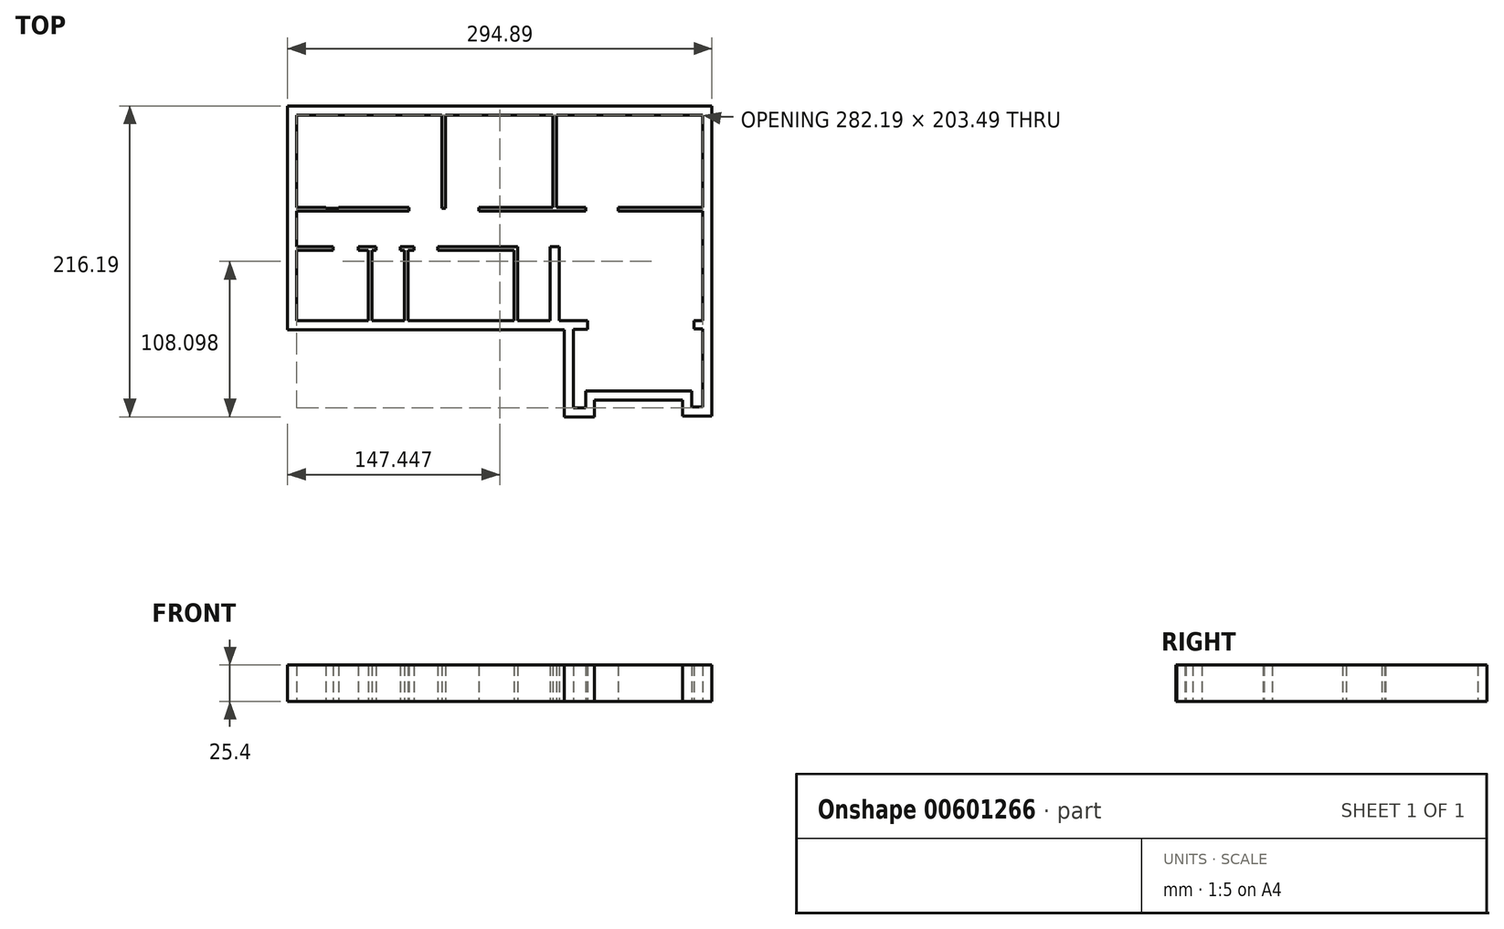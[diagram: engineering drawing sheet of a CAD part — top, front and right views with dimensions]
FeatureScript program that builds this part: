
annotation { "Feature Type Name" : "Feature", "Feature Type Description" : "" }
export const myFeature = defineFeature(function(context is Context, id is Id, definition is map)
    precondition{}
    {
        {
            var Q0;
            Q0=qCreatedBy(makeId("Top.planeOp"),FACE);
            var sketch = newSketch(context, id + "F0", { "sketchPlane" : qUnion([Q0])});
            skLineSegment(sketch, "E0.bottom", {"start": v(0, 66.8) * mm, "end": v(282.2, 66.8) * mm});
            skLineSegment(sketch, "E0.left", {"start": v(0, 66.8) * mm, "end": v(0, -76.2) * mm});
            skLineSegment(sketch, "E0.right", {"start": v(282.2, 66.8) * mm, "end": v(282.2, -81.91) * mm});
            skPoint(sketch, "E1.oppositeSnap0", {"position": v(180.6, 0) * mm});
            skLineSegment(sketch, "E1.right", {"start": v(282.2, 2.54) * mm, "end": v(282.2, 0) * mm});
            skLineSegment(sketch, "E2.bottom", {"start": v(100.84, 66.8) * mm, "end": v(103.38, 66.8) * mm});
            skLineSegment(sketch, "E2.top", {"start": v(100.84, 2.08) * mm, "end": v(103.38, 2.08) * mm});
            skLineSegment(sketch, "E2.left", {"start": v(100.84, 66.8) * mm, "end": v(100.84, 2.08) * mm});
            skLineSegment(sketch, "E2.right", {"start": v(103.38, 66.8) * mm, "end": v(103.38, 2.08) * mm});
            skLineSegment(sketch, "E3.bottom", {"start": v(178.05, 66.8) * mm, "end": v(180.6, 66.8) * mm});
            skLineSegment(sketch, "E3.top", {"start": v(178.05, 2.54) * mm, "end": v(180.6, 2.54) * mm});
            skLineSegment(sketch, "E3.left", {"start": v(178.05, 66.8) * mm, "end": v(178.05, 2.54) * mm});
            skLineSegment(sketch, "E3.right", {"start": v(180.6, 66.8) * mm, "end": v(180.6, 2.54) * mm});
            skLineSegment(sketch, "E4.left", {"start": v(0, -24.64) * mm, "end": v(0, -27.18) * mm});
            skLineSegment(sketch, "E5.bottom", {"start": v(176.02, -24.64) * mm, "end": v(182.37, -24.64) * mm});
            skLineSegment(sketch, "E5.top", {"start": v(176.02, -76.2) * mm, "end": v(182.37, -76.2) * mm});
            skLineSegment(sketch, "E5.left", {"start": v(176.02, -24.64) * mm, "end": v(176.02, -76.2) * mm});
            skLineSegment(sketch, "E5.right", {"start": v(182.37, -24.64) * mm, "end": v(182.37, -76.2) * mm});
            skLineSegment(sketch, "E6", {"start": v(0, -76.2) * mm, "end": v(176.02, -76.2) * mm});
            skLineSegment(sketch, "E7.bottom", {"start": v(153.67, -27.18) * mm, "end": v(151.13, -27.18) * mm});
            skLineSegment(sketch, "E7.top", {"start": v(153.67, -76.2) * mm, "end": v(151.13, -76.2) * mm});
            skLineSegment(sketch, "E7.left", {"start": v(153.67, -27.18) * mm, "end": v(153.67, -76.2) * mm});
            skLineSegment(sketch, "E7.right", {"start": v(151.13, -27.18) * mm, "end": v(151.13, -76.2) * mm});
            skLineSegment(sketch, "E8.top", {"start": v(74.68, -76.2) * mm, "end": v(77.22, -76.2) * mm});
            skLineSegment(sketch, "E8.left", {"start": v(74.68, -25.1) * mm, "end": v(74.68, -76.2) * mm});
            skLineSegment(sketch, "E8.right", {"start": v(77.22, -25.1) * mm, "end": v(77.22, -76.2) * mm});
            skLineSegment(sketch, "E9.bottom", {"start": v(49.78, -27.18) * mm, "end": v(52.32, -27.18) * mm});
            skLineSegment(sketch, "E9.top", {"start": v(49.78, -76.2) * mm, "end": v(52.32, -76.2) * mm});
            skLineSegment(sketch, "E9.left", {"start": v(49.78, -27.18) * mm, "end": v(49.78, -76.2) * mm});
            skLineSegment(sketch, "E9.right", {"start": v(52.32, -27.18) * mm, "end": v(52.32, -76.2) * mm});
            skLineSegment(sketch, "E10", {"start": v(200.7, -125.1) * mm, "end": v(200.7, -125.1) * mm});
            skLineSegment(sketch, "E11", {"start": v(200.7, -125.1) * mm, "end": v(274.57, -125.1) * mm});
            skLineSegment(sketch, "E12", {"start": v(274.57, -125.1) * mm, "end": v(274.57, -136.17) * mm});
            skLineSegment(sketch, "E13", {"start": v(274.57, -136.17) * mm, "end": v(282.2, -136.17) * mm});
            skLineSegment(sketch, "E14", {"start": v(282.2, -136.17) * mm, "end": v(282.2, -81.92) * mm});
            skLineSegment(sketch, "E15.bottom", {"start": v(182.37, -76.2) * mm, "end": v(202.18, -76.2) * mm});
            skLineSegment(sketch, "E15.top", {"start": v(182.37, -76.2) * mm, "end": v(202.18, -76.2) * mm});
            skLineSegment(sketch, "E15.left", {"start": v(182.37, -76.2) * mm, "end": v(182.37, -76.2) * mm});
            skLineSegment(sketch, "E15.right", {"start": v(202.18, -76.2) * mm, "end": v(202.18, -76.2) * mm});
            skPoint(sketch, "E16.oppositeSnap0", {"position": v(192.28, -76.2) * mm});
            skLineSegment(sketch, "E16.bottom", {"start": v(282.2, -81.92) * mm, "end": v(276.23, -81.92) * mm});
            skLineSegment(sketch, "E16.top", {"start": v(282.2, -76.2) * mm, "end": v(276.23, -76.2) * mm});
            skLineSegment(sketch, "E16.left", {"start": v(282.2, -81.92) * mm, "end": v(282.2, -76.2) * mm});
            skLineSegment(sketch, "E16.right", {"start": v(276.23, -81.92) * mm, "end": v(276.23, -76.2) * mm});
            skLineSegment(sketch, "E17", {"start": v(192.28, -76.2) * mm, "end": v(192.28, -136.69) * mm});
            skLineSegment(sketch, "E18.bottom", {"start": v(153.67, -27.18) * mm, "end": v(97.81, -27.18) * mm});
            skLineSegment(sketch, "E18.top", {"start": v(153.67, -24.64) * mm, "end": v(97.81, -24.64) * mm});
            skLineSegment(sketch, "E18.left", {"start": v(153.67, -27.18) * mm, "end": v(153.67, -24.64) * mm});
            skLineSegment(sketch, "E18.right", {"start": v(97.81, -27.18) * mm, "end": v(97.81, -24.64) * mm});
            skLineSegment(sketch, "E19", {"start": v(202.18, -76.2) * mm, "end": v(202.18, -82.17) * mm});
            skLineSegment(sketch, "E20", {"start": v(202.18, -82.17) * mm, "end": v(192.28, -82.17) * mm});
            skLineSegment(sketch, "E21.bottom", {"start": v(55.18, -27.18) * mm, "end": v(42.64, -27.18) * mm});
            skLineSegment(sketch, "E21.top", {"start": v(55.18, -24.64) * mm, "end": v(42.64, -24.64) * mm});
            skLineSegment(sketch, "E21.left", {"start": v(55.18, -27.18) * mm, "end": v(55.18, -24.64) * mm});
            skLineSegment(sketch, "E21.right", {"start": v(42.64, -27.18) * mm, "end": v(42.64, -24.64) * mm});
            skLineSegment(sketch, "E22.bottom", {"start": v(25.37, -27.18) * mm, "end": v(0, -27.18) * mm});
            skLineSegment(sketch, "E22.top", {"start": v(25.37, -24.64) * mm, "end": v(0, -24.64) * mm});
            skLineSegment(sketch, "E22.left", {"start": v(25.37, -27.18) * mm, "end": v(25.37, -24.64) * mm});
            skLineSegment(sketch, "E22.right", {"start": v(0, -27.18) * mm, "end": v(0, -24.64) * mm});
            skLineSegment(sketch, "E23.bottom", {"start": v(71.89, -27.18) * mm, "end": v(81.55, -27.18) * mm});
            skLineSegment(sketch, "E23.top", {"start": v(71.89, -24.64) * mm, "end": v(81.55, -24.64) * mm});
            skLineSegment(sketch, "E23.left", {"start": v(71.89, -27.18) * mm, "end": v(71.89, -24.64) * mm});
            skLineSegment(sketch, "E23.right", {"start": v(81.55, -27.18) * mm, "end": v(81.55, -24.64) * mm});
            skLineSegment(sketch, "E24.bottom", {"start": v(0, 0) * mm, "end": v(78.08, 0) * mm});
            skLineSegment(sketch, "E24.top", {"start": v(0, 2.54) * mm, "end": v(78.08, 2.54) * mm});
            skLineSegment(sketch, "E24.left", {"start": v(0, 0) * mm, "end": v(0, 2.54) * mm});
            skLineSegment(sketch, "E24.right", {"start": v(78.08, 0) * mm, "end": v(78.08, 2.54) * mm});
            skLineSegment(sketch, "E25.bottom", {"start": v(126.64, 2.54) * mm, "end": v(200.91, 2.54) * mm});
            skLineSegment(sketch, "E25.top", {"start": v(126.64, 0) * mm, "end": v(200.91, 0) * mm});
            skLineSegment(sketch, "E25.left", {"start": v(126.64, 2.54) * mm, "end": v(126.64, 0) * mm});
            skLineSegment(sketch, "E25.right", {"start": v(200.91, 2.54) * mm, "end": v(200.91, 0) * mm});
            skLineSegment(sketch, "E26.bottom", {"start": v(223.27, 2.54) * mm, "end": v(282.2, 2.54) * mm});
            skLineSegment(sketch, "E26.top", {"start": v(223.27, 0) * mm, "end": v(282.2, 0) * mm});
            skLineSegment(sketch, "E26.left", {"start": v(223.27, 2.54) * mm, "end": v(223.27, 0) * mm});
            skLineSegment(sketch, "E27", {"start": v(192.28, -136.69) * mm, "end": v(200.7, -136.69) * mm});
            skLineSegment(sketch, "E28", {"start": v(200.7, -136.69) * mm, "end": v(200.7, -125.1) * mm});
            skLineSegment(sketch, "E29.0", {"start": v(-6.35, -82.55) * mm, "end": v(185.93, -82.55) * mm});
            skLineSegment(sketch, "E29.1", {"start": v(207.04, -131.45) * mm, "end": v(268.22, -131.45) * mm});
            skLineSegment(sketch, "E29.2", {"start": v(207.04, -143.04) * mm, "end": v(207.04, -131.45) * mm});
            skLineSegment(sketch, "E29.3", {"start": v(185.93, -143.04) * mm, "end": v(207.04, -143.04) * mm});
            skLineSegment(sketch, "E29.4", {"start": v(185.93, -82.55) * mm, "end": v(185.93, -143.04) * mm});
            skLineSegment(sketch, "E29.5", {"start": v(268.22, -131.45) * mm, "end": v(268.22, -142.52) * mm});
            skLineSegment(sketch, "E29.6", {"start": v(268.22, -142.52) * mm, "end": v(288.54, -142.52) * mm});
            skLineSegment(sketch, "E29.7", {"start": v(288.54, -142.52) * mm, "end": v(288.54, -81.91) * mm});
            skLineSegment(sketch, "E29.8", {"start": v(288.54, 73.15) * mm, "end": v(288.54, -81.91) * mm});
            skLineSegment(sketch, "E29.9", {"start": v(-6.35, 73.15) * mm, "end": v(288.54, 73.15) * mm});
            skLineSegment(sketch, "E29.10", {"start": v(-6.35, 73.15) * mm, "end": v(-6.35, -82.55) * mm});
            skLineSegment(sketch, "E30.top", {"start": v(29.49, 2.54) * mm, "end": v(68.2, 2.54) * mm});
            skLineSegment(sketch, "E31.bottom", {"start": v(100.43, 2.08) * mm, "end": v(104.29, 2.08) * mm});
            skLineSegment(sketch, "E31.top", {"start": v(100.43, 0) * mm, "end": v(104.29, 0) * mm});
            skLineSegment(sketch, "E31.left", {"start": v(100.43, 2.08) * mm, "end": v(100.43, 0) * mm});
            skLineSegment(sketch, "E31.right", {"start": v(104.29, 2.08) * mm, "end": v(104.29, 0) * mm});
            skLineSegment(sketch, "E32.bottom", {"start": v(222.24, -86.9) * mm, "end": v(257.3, -86.9) * mm});
            skLineSegment(sketch, "E32.top", {"start": v(222.24, -110.13) * mm, "end": v(257.3, -110.13) * mm});
            skLineSegment(sketch, "E32.left", {"start": v(222.24, -86.9) * mm, "end": v(222.24, -110.13) * mm});
            skLineSegment(sketch, "E32.right", {"start": v(257.3, -86.9) * mm, "end": v(257.3, -110.13) * mm});
            skLineSegment(sketch, "E33.bottom", {"start": v(264.03, -86.9) * mm, "end": v(213.74, -86.9) * mm});
            skLineSegment(sketch, "E33.top", {"start": v(264.03, -110.13) * mm, "end": v(213.74, -110.13) * mm});
            skLineSegment(sketch, "E33.left", {"start": v(264.03, -86.9) * mm, "end": v(264.03, -110.13) * mm});
            skLineSegment(sketch, "E33.right", {"start": v(213.74, -86.9) * mm, "end": v(213.74, -110.13) * mm});
            skLineSegment(sketch, "E34.top", {"start": v(68.68, 2.54) * mm, "end": v(78.08, 2.54) * mm});
            skLineSegment(sketch, "E35.bottom", {"start": v(0, 17.2) * mm, "end": v(19.66, 17.2) * mm});
            skLineSegment(sketch, "E35.top", {"start": v(0, 18.17) * mm, "end": v(19.66, 18.17) * mm});
            skLineSegment(sketch, "E35.left", {"start": v(0, 17.2) * mm, "end": v(0, 18.17) * mm});
            skLineSegment(sketch, "E35.right", {"start": v(19.66, 17.2) * mm, "end": v(19.66, 18.17) * mm});
            skLineSegment(sketch, "E36.bottom", {"start": v(19.66, 17.2) * mm, "end": v(18.7, 17.2) * mm});
            skLineSegment(sketch, "E36.top", {"start": v(19.66, 2.54) * mm, "end": v(18.7, 2.54) * mm});
            skLineSegment(sketch, "E36.left", {"start": v(19.66, 17.2) * mm, "end": v(19.66, 2.54) * mm});
            skLineSegment(sketch, "E36.right", {"start": v(18.7, 17.2) * mm, "end": v(18.7, 2.54) * mm});
            skLineSegment(sketch, "E37.bottom", {"start": v(20.07, 12.11) * mm, "end": v(29.22, 12.11) * mm});
            skLineSegment(sketch, "E37.top", {"start": v(20.07, 1.95) * mm, "end": v(29.22, 1.95) * mm});
            skLineSegment(sketch, "E37.left", {"start": v(20.07, 12.11) * mm, "end": v(20.07, 1.95) * mm});
            skLineSegment(sketch, "E37.right", {"start": v(29.22, 12.11) * mm, "end": v(29.22, 1.95) * mm});
            skLineSegment(sketch, "E38.bottom", {"start": v(126.33, 65.86) * mm, "end": v(177.13, 65.86) * mm});
            skLineSegment(sketch, "E38.top", {"start": v(126.33, 42.64) * mm, "end": v(177.13, 42.64) * mm});
            skLineSegment(sketch, "E38.left", {"start": v(126.33, 65.86) * mm, "end": v(126.33, 42.64) * mm});
            skLineSegment(sketch, "E38.right", {"start": v(177.13, 65.86) * mm, "end": v(177.13, 42.64) * mm});
            skLineSegment(sketch, "E39.bottom", {"start": v(126.33, 26.75) * mm, "end": v(177.13, 26.75) * mm});
            skLineSegment(sketch, "E39.top", {"start": v(126.33, 3.53) * mm, "end": v(177.13, 3.53) * mm});
            skLineSegment(sketch, "E39.left", {"start": v(126.33, 26.75) * mm, "end": v(126.33, 3.53) * mm});
            skLineSegment(sketch, "E39.right", {"start": v(177.13, 26.75) * mm, "end": v(177.13, 3.53) * mm});
            skLineSegment(sketch, "E40.bottom", {"start": v(166.57, 40.84) * mm, "end": v(174.7, 40.84) * mm});
            skLineSegment(sketch, "E40.top", {"start": v(166.57, 30.17) * mm, "end": v(174.7, 30.17) * mm});
            skLineSegment(sketch, "E40.left", {"start": v(166.57, 40.84) * mm, "end": v(166.57, 30.17) * mm});
            skLineSegment(sketch, "E40.right", {"start": v(174.7, 40.84) * mm, "end": v(174.7, 30.17) * mm});
            skLineSegment(sketch, "E41", {"start": v(282.2, 48.76) * mm, "end": v(198.74, 48.76) * mm});
            skLineSegment(sketch, "E42", {"start": v(198.74, 48.76) * mm, "end": v(198.74, 2.54) * mm});
            skLineSegment(sketch, "E43.bottom", {"start": v(0, 61.58) * mm, "end": v(57.35, 61.58) * mm});
            skLineSegment(sketch, "E43.top", {"start": v(0, 22.7) * mm, "end": v(57.35, 22.7) * mm});
            skLineSegment(sketch, "E43.left", {"start": v(0, 61.58) * mm, "end": v(0, 22.7) * mm});
            skLineSegment(sketch, "E43.right", {"start": v(57.35, 61.58) * mm, "end": v(57.35, 22.7) * mm});
            skLineSegment(sketch, "E44.bottom", {"start": v(77.67, 66.8) * mm, "end": v(100.84, 66.8) * mm});
            skLineSegment(sketch, "E44.top", {"start": v(77.67, 48.32) * mm, "end": v(100.84, 48.32) * mm});
            skLineSegment(sketch, "E44.left", {"start": v(77.67, 66.8) * mm, "end": v(77.67, 48.32) * mm});
            skLineSegment(sketch, "E44.right", {"start": v(100.84, 66.8) * mm, "end": v(100.84, 48.32) * mm});
            skLineSegment(sketch, "E45.top", {"start": v(97.81, -27.18) * mm, "end": v(153.67, -27.18) * mm});
            skLineSegment(sketch, "E45.left", {"start": v(97.81, -46.23) * mm, "end": v(97.81, -27.18) * mm});
            skLineSegment(sketch, "E45.right", {"start": v(153.67, -46.23) * mm, "end": v(153.67, -27.18) * mm});
            skLineSegment(sketch, "E46.top", {"start": v(97.81, -64.79) * mm, "end": v(151.13, -64.79) * mm});
            skLineSegment(sketch, "E46.left", {"start": v(97.81, -46.23) * mm, "end": v(97.81, -64.79) * mm});
            skLineSegment(sketch, "E46.right", {"start": v(151.13, -46.23) * mm, "end": v(151.13, -64.79) * mm});
            skLineSegment(sketch, "E47", {"start": v(176.02, -24.64) * mm, "end": v(153.67, -24.64) * mm});
            skLineSegment(sketch, "E48", {"start": v(153.67, -31.2) * mm, "end": v(176.02, -31.2) * mm});
            skLineSegment(sketch, "E49", {"start": v(153.67, -37.95) * mm, "end": v(176.02, -37.95) * mm});
            skLineSegment(sketch, "E50", {"start": v(153.67, -44.5) * mm, "end": v(176.02, -44.5) * mm});
            skLineSegment(sketch, "E51", {"start": v(153.67, -51.69) * mm, "end": v(176.02, -51.69) * mm});
            skLineSegment(sketch, "E52", {"start": v(153.67, -58.73) * mm, "end": v(176.02, -58.73) * mm});
            skLineSegment(sketch, "E53", {"start": v(153.67, -65.49) * mm, "end": v(176.02, -65.49) * mm});
            skLineSegment(sketch, "E54", {"start": v(153.67, -72.24) * mm, "end": v(176.02, -72.24) * mm});
            skLineSegment(sketch, "E55", {"start": v(223.27, 0) * mm, "end": v(223.27, -18.33) * mm});
            skLineSegment(sketch, "E56", {"start": v(223.27, -18.33) * mm, "end": v(261.3, -18.33) * mm});
            skLineSegment(sketch, "E57", {"start": v(261.3, -18.33) * mm, "end": v(261.3, -64.6) * mm});
            skLineSegment(sketch, "E58", {"start": v(261.3, -64.6) * mm, "end": v(282.2, -64.6) * mm});
            skLineSegment(sketch, "E59.bottom", {"start": v(182.37, -29.67) * mm, "end": v(194.25, -29.67) * mm});
            skLineSegment(sketch, "E59.top", {"start": v(182.37, -66.02) * mm, "end": v(194.25, -66.02) * mm});
            skLineSegment(sketch, "E59.left", {"start": v(182.37, -29.67) * mm, "end": v(182.37, -66.02) * mm});
            skLineSegment(sketch, "E59.right", {"start": v(194.25, -29.67) * mm, "end": v(194.25, -66.02) * mm});
            skSolve(sketch);
        }
        {
            var Q0;
            {var subQ7=sQuery(id+"F0.wireOp",EDGE,"E5.top");Q0=makeQuery(id+"F0.imprint","IMPRINT",FACE,{"disambiguationData":[TD([[makeQuery(id+"F0.imprint","IMPRINT",EDGE,{"derivedFrom":subQ7}),-1.0]])]});}
            var Q1;
            {var subQ5=sQuery(id+"F0.wireOp",EDGE,"E24.bottom");Q1=makeQuery(id+"F0.imprint","IMPRINT",FACE,{"disambiguationData":[TD([[makeQuery(id+"F0.imprint","IMPRINT",EDGE,{"derivedFrom":subQ5}),1.0]])]});}
            var Q2;
            {var subQ4=sQuery(id+"F0.wireOp",EDGE,"E2.top");Q2=makeQuery(id+"F0.imprint","IMPRINT",FACE,{"disambiguationData":[TD([[makeQuery(id+"F0.imprint","IMPRINT",EDGE,{"derivedFrom":subQ4}),1.0]])]});}
            var Q3;
            Q3=makeQuery(id+"F0.imprint","IMPRINT",FACE,{"disambiguationData":[TD([[makeQuery(id+"F0.imprint","IMPRINT",EDGE,{"derivedFrom":sQuery(id+"F0.wireOp",EDGE,"rbAKpTVN-eiLL-Qd1i-zqsu-B6mDTiPCECB1.top")}),1.0]])]});
            var Q4;
            {var subQ3=sQuery(id+"F0.wireOp",EDGE,"E3.top");Q4=makeQuery(id+"F0.imprint","IMPRINT",FACE,{"disambiguationData":[TD([[makeQuery(id+"F0.imprint","IMPRINT",EDGE,{"derivedFrom":subQ3}),-1.0]])]});}
            var Q5;
            Q5=makeQuery(id+"F0.imprint","IMPRINT",FACE,{"disambiguationData":[TD([[makeQuery(id+"F0.imprint","IMPRINT",EDGE,{"derivedFrom":sQuery(id+"F0.wireOp",EDGE,"E3.top")}),1.0]])]});
            var Q6;
            {var subQ2=sQuery(id+"F0.wireOp",EDGE,"E26.bottom");Q6=makeQuery(id+"F0.imprint","IMPRINT",FACE,{"disambiguationData":[TD([[makeQuery(id+"F0.imprint","IMPRINT",EDGE,{"derivedFrom":subQ2}),-1.0]])]});}
            var Q7;
            {var subQ5=sQuery(id+"F0.wireOp",EDGE,"E5.bottom");Q7=makeQuery(id+"F0.imprint","IMPRINT",FACE,{"disambiguationData":[TD([[makeQuery(id+"F0.imprint","IMPRINT",EDGE,{"derivedFrom":subQ5}),-1.0]])]});}
            var Q8;
            {var subQ0=sQuery(id+"F0.wireOp",EDGE,"E19");Q8=makeQuery(id+"F0.imprint","IMPRINT",FACE,{"disambiguationData":[TD([[makeQuery(id+"F0.imprint","IMPRINT",EDGE,{"derivedFrom":subQ0}),-1.0]])]});}
            var Q9;
            {var subQ0=sQuery(id+"F0.wireOp",EDGE,"E16.bottom");Q9=makeQuery(id+"F0.imprint","IMPRINT",FACE,{"disambiguationData":[TD([[makeQuery(id+"F0.imprint","IMPRINT",EDGE,{"derivedFrom":subQ0}),-1.0]])]});}
            var Q10;
            {var subQ1=sQuery(id+"F0.wireOp",EDGE,"E7.bottom");Q10=makeQuery(id+"F0.imprint","IMPRINT",FACE,{"disambiguationData":[TD([[makeQuery(id+"F0.imprint","IMPRINT",EDGE,{"derivedFrom":subQ1}),1.0]])]});}
            var Q11;
            Q11=makeQuery(id+"F0.imprint","IMPRINT",FACE,{"disambiguationData":[TD([[makeQuery(id+"F0.imprint","IMPRINT",EDGE,{"derivedFrom":sQuery(id+"F0.wireOp",EDGE,"E7.bottom")}),-1.0]])]});
            var Q12;
            {var subQ0=sQuery(id+"F0.wireOp",EDGE,"E8.right");var subQ1=sQuery(id+"F0.wireOp",EDGE,"E6");var subQ2=makeQuery(id+"F0.imprint","INTERSECT",VERTEX,{"derivedFrom":[subQ1,subQ0]});Q12=makeQuery(id+"F0.imprint","IMPRINT",FACE,{"disambiguationData":[TD([[makeQuery(id+"F0.imprint","IMPRINT",EDGE,{"disambiguationData":[TD([[subQ2,1.0]])],"derivedFrom":subQ1}),1.0]])]});}
            var Q13;
            Q13=makeQuery(id+"F0.imprint","IMPRINT",FACE,{"disambiguationData":[TD([[makeQuery(id+"F0.imprint","IMPRINT",EDGE,{"derivedFrom":sQuery(id+"F0.wireOp",EDGE,"E23.top")}),-1.0]])]});
            var Q14;
            Q14=makeQuery(id+"F0.imprint","IMPRINT",FACE,{"disambiguationData":[TD([[makeQuery(id+"F0.imprint","IMPRINT",EDGE,{"derivedFrom":sQuery(id+"F0.wireOp",EDGE,"E9.bottom")}),-1.0]])]});
            var Q15;
            {var subQ0=sQuery(id+"F0.wireOp",EDGE,"E9.bottom");Q15=makeQuery(id+"F0.imprint","IMPRINT",FACE,{"disambiguationData":[TD([[makeQuery(id+"F0.imprint","IMPRINT",EDGE,{"derivedFrom":subQ0}),1.0]])]});}
            var Q16;
            {var subQ0=sQuery(id+"F0.wireOp",EDGE,"E22.bottom");Q16=makeQuery(id+"F0.imprint","IMPRINT",FACE,{"disambiguationData":[TD([[makeQuery(id+"F0.imprint","IMPRINT",EDGE,{"derivedFrom":subQ0}),-1.0]])]});}
            extrude(context, id + "F1", {"entities" : qUnion([Q0, Q1, Q2, Q3, Q4, Q5, Q6, Q7, Q8, Q9, Q10, Q11, Q12, Q13, Q14, Q15, Q16]), "depth" : 25.4 * mm, "offsetDistance" : 25.4 * mm});
        }
    });
